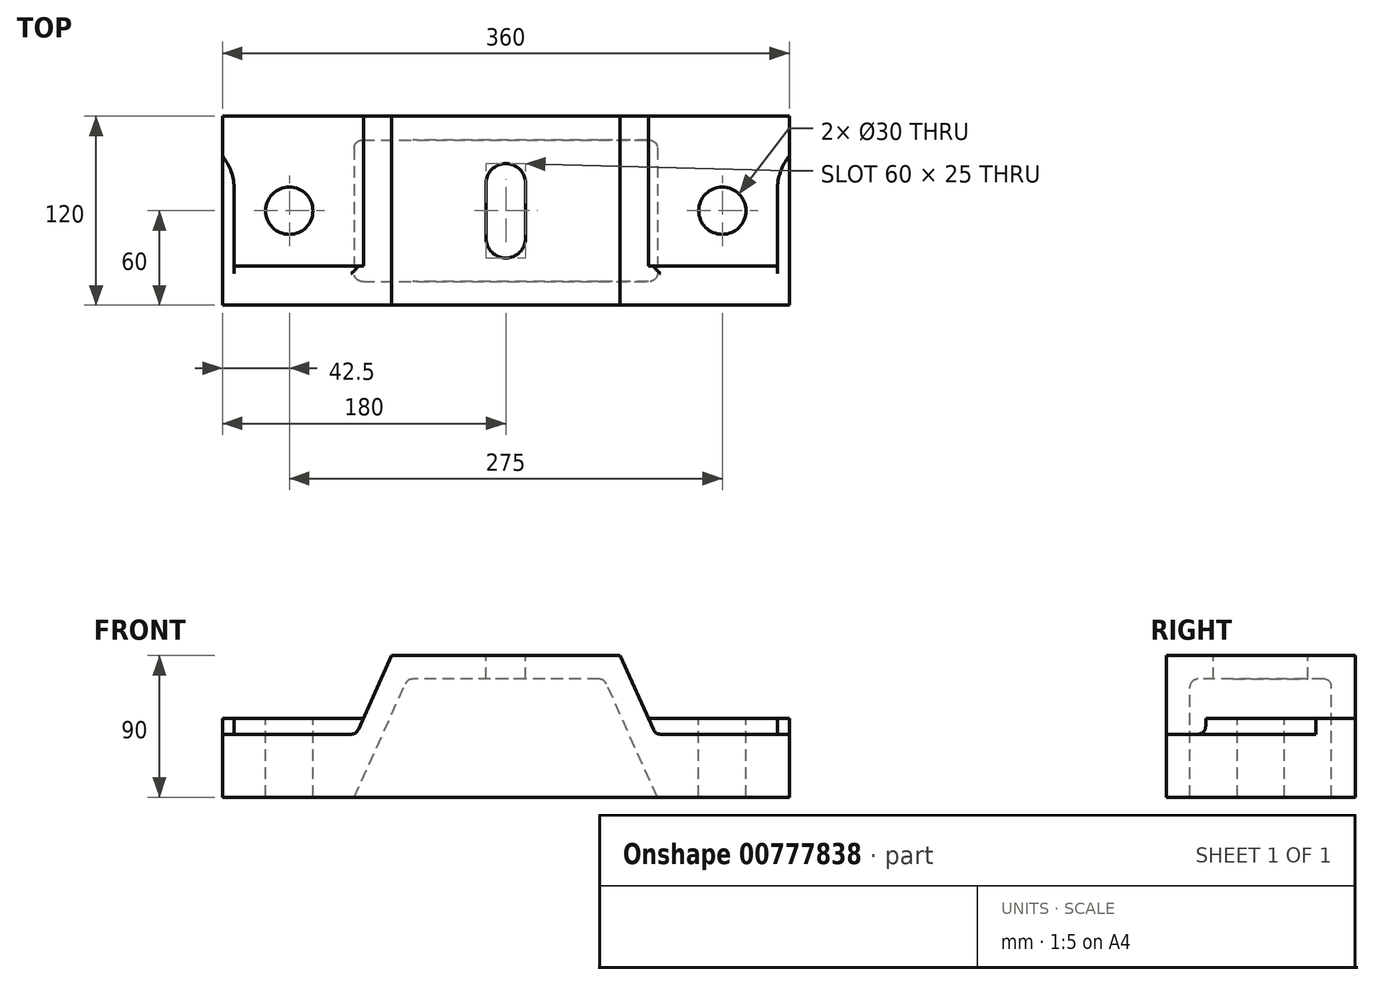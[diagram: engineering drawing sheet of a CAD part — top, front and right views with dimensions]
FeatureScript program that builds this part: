
annotation { "Feature Type Name" : "Feature", "Feature Type Description" : "" }
export const myFeature = defineFeature(function(context is Context, id is Id, definition is map)
    precondition{}
    {
        {
            var Q0;
            Q0=qCreatedBy(makeId("Front.planeOp"),FACE);
            var sketch = newSketch(context, id + "F0", { "sketchPlane" : qUnion([Q0])});
            skLineSegment(sketch, "E0", {"start": v(0, 0) * mm, "end": v(-180, 0) * mm});
            skLineSegment(sketch, "E1", {"start": v(-180, 0) * mm, "end": v(-180, 50) * mm});
            skLineSegment(sketch, "E2", {"start": v(-180, 50) * mm, "end": v(-90.5, 50) * mm});
            skLineSegment(sketch, "E3", {"start": v(-90.5, 50) * mm, "end": v(-72.5, 90) * mm});
            skLineSegment(sketch, "E4", {"start": v(-72.5, 90) * mm, "end": v(0, 90) * mm});
            skLineSegment(sketch, "E5", {"start": v(-90.5, 50) * mm, "end": v(-95, 40) * mm, "construction": true});
            skLineSegment(sketch, "E6.MirrorCS", {"start": v(72.5, 90) * mm, "end": v(0, 90) * mm});
            skLineSegment(sketch, "E7.MirrorCS", {"start": v(90.5, 50) * mm, "end": v(72.5, 90) * mm});
            skLineSegment(sketch, "E8.MirrorCS", {"start": v(180, 50) * mm, "end": v(90.5, 50) * mm});
            skLineSegment(sketch, "E9.MirrorCS", {"start": v(180, 0) * mm, "end": v(180, 50) * mm});
            skLineSegment(sketch, "E10.MirrorCS", {"start": v(0, 0) * mm, "end": v(180, 0) * mm});
            skSolve(sketch);
        }
        {
            var Q0;
            Q0=makeQuery(id+"F0.imprint","IMPRINT",FACE,{"disambiguationData":[TD([[makeQuery(id+"F0.imprint","IMPRINT",EDGE,{"derivedFrom":sQuery(id+"F0.wireOp",EDGE,"E0")}),-1.0]])]});
            extrude(context, id + "F1", {"entities" : qUnion([Q0]), "endBound" : BoundingType.SYMMETRIC, "depth" : 120 * mm, "offsetDistance" : 25 * mm});
        }
        {
            var Q0;
            Q0=makeQuery(id+"F1.opExtrude","CAP_FACE",FACE,{"disambiguationData":[OSD([sQuery(id+"F0.wireOp",EDGE,"E0"),sQuery(id+"F0.wireOp",EDGE,"E1"),sQuery(id+"F0.wireOp",EDGE,"E2"),sQuery(id+"F0.wireOp",EDGE,"E3"),sQuery(id+"F0.wireOp",EDGE,"E4"),sQuery(id+"F0.wireOp",EDGE,"E6.MirrorCS"),sQuery(id+"F0.wireOp",EDGE,"E7.MirrorCS"),sQuery(id+"F0.wireOp",EDGE,"E8.MirrorCS"),sQuery(id+"F0.wireOp",EDGE,"E9.MirrorCS"),sQuery(id+"F0.wireOp",EDGE,"E10.MirrorCS")])],"isStart":false});
            var sketch = newSketch(context, id + "F2", { "sketchPlane" : qUnion([Q0])});
            skLineSegment(sketch, "E11", {"start": v(-90.5, 50) * mm, "end": v(-95, 40) * mm});
            skLineSegment(sketch, "E12", {"start": v(-95, 40) * mm, "end": v(-180, 40) * mm});
            skLineSegment(sketch, "E13", {"start": v(-180, 40) * mm, "end": v(-180, 50) * mm});
            skLineSegment(sketch, "E14", {"start": v(-180, 50) * mm, "end": v(-90.5, 50) * mm});
            skLineSegment(sketch, "E15.MirrorCS", {"start": v(90.5, 50) * mm, "end": v(95, 40) * mm});
            skLineSegment(sketch, "E16.MirrorCS", {"start": v(95, 40) * mm, "end": v(180, 40) * mm});
            skLineSegment(sketch, "E17.MirrorCS", {"start": v(180, 40) * mm, "end": v(180, 50) * mm});
            skLineSegment(sketch, "E18.MirrorCS", {"start": v(180, 50) * mm, "end": v(90.5, 50) * mm});
            skSolve(sketch);
        }
        {
            var Q0;
            Q0 = qSketchRegion(id + "F2", true);
            extrude(context, id + "F3", {"entities" : qUnion([Q0]), "operationType" : NewBodyOperationType.REMOVE, "oppositeDirection" : true, "depth" : 25 * mm, "offsetDistance" : 25 * mm});
        }
        {
            var Q0;
            Q0=makeQuery(id+"F3.boolean.opBoolean","COPY",FACE,{"derivedFrom":makeQuery(id+"F3.opExtrude","CAP_FACE",FACE,{"disambiguationData":[OSD([sQuery(id+"F2.wireOp",EDGE,"E11"),sQuery(id+"F2.wireOp",EDGE,"E12"),sQuery(id+"F2.wireOp",EDGE,"E13"),sQuery(id+"F2.wireOp",EDGE,"E14")])],"isStart":false})});
            var sketch = newSketch(context, id + "F4", { "sketchPlane" : qUnion([Q0])});
            skLineSegment(sketch, "E19.bottom", {"start": v(-180, 40) * mm, "end": v(-172.5, 40) * mm});
            skLineSegment(sketch, "E19.top", {"start": v(-180, 50) * mm, "end": v(-172.5, 50) * mm});
            skLineSegment(sketch, "E19.left", {"start": v(-180, 40) * mm, "end": v(-180, 50) * mm});
            skLineSegment(sketch, "E19.right", {"start": v(-172.5, 40) * mm, "end": v(-172.5, 50) * mm});
            skLineSegment(sketch, "E20.MirrorCS", {"start": v(172.5, 40) * mm, "end": v(172.5, 50) * mm});
            skLineSegment(sketch, "E21.MirrorCS", {"start": v(180, 40) * mm, "end": v(172.5, 40) * mm});
            skLineSegment(sketch, "E22.MirrorCS", {"start": v(180, 40) * mm, "end": v(180, 50) * mm});
            skLineSegment(sketch, "E23.MirrorCS", {"start": v(180, 50) * mm, "end": v(172.5, 50) * mm});
            skSolve(sketch);
        }
        {
            var Q0;
            Q0 = qSketchRegion(id + "F4", true);
            extrude(context, id + "F5", {"entities" : qUnion([Q0]), "operationType" : NewBodyOperationType.REMOVE, "oppositeDirection" : true, "depth" : 70 * mm, "offsetDistance" : 25 * mm});
        }
        {
            var Q0;
            Q0=makeQuery(id+"F5.boolean.opBoolean","COPY",EDGE,{"derivedFrom":makeQuery(id+"F5.opExtrude","CAP_EDGE",EDGE,{"disambiguationData":[OSD([sQuery(id+"F4.wireOp",EDGE,"E20.MirrorCS")])],"isStart":true})});
            var Q1;
            Q1=makeQuery(id+"F5.boolean.opBoolean","COPY",EDGE,{"derivedFrom":makeQuery(id+"F5.opExtrude","CAP_EDGE",EDGE,{"disambiguationData":[OSD([sQuery(id+"F4.wireOp",EDGE,"E20.MirrorCS")])],"isStart":false})});
            var Q2;
            Q2=makeQuery(id+"F5.boolean.opBoolean","COPY",EDGE,{"derivedFrom":makeQuery(id+"F5.opExtrude","CAP_EDGE",EDGE,{"disambiguationData":[OSD([sQuery(id+"F4.wireOp",EDGE,"E19.right")])],"isStart":true})});
            var Q3;
            Q3=makeQuery(id+"F5.boolean.opBoolean","COPY",EDGE,{"derivedFrom":makeQuery(id+"F5.opExtrude","CAP_EDGE",EDGE,{"disambiguationData":[OSD([sQuery(id+"F4.wireOp",EDGE,"E19.right")])],"isStart":false})});
            fillet(context, id + "F6", {"entities" : qUnion([Q0, Q1, Q2, Q3]), "radius" : 35 * mm, "tangentPropagation" : true, "allowEdgeOverflow" : false});
        }
        {
            var Q0;
            Q0=makeQuery(id+"F3.boolean.opBoolean","COPY",EDGE,{"derivedFrom":makeQuery(id+"F3.opExtrude","CAP_EDGE",EDGE,{"disambiguationData":[OSD([sQuery(id+"F2.wireOp",EDGE,"E16.MirrorCS")])],"isStart":false})});
            var Q1;
            Q1=makeQuery(id+"F3.boolean.opBoolean","COPY",EDGE,{"derivedFrom":makeQuery(id+"F3.opExtrude","SWEPT_EDGE",EDGE,{"disambiguationData":[OSD([sQuery(id+"F2.wireOp",EDGE,"E15.MirrorCS"),sQuery(id+"F2.wireOp",EDGE,"E16.MirrorCS")])]})});
            var Q2;
            Q2=makeQuery(id+"FUGxs0qXSOKFCMJ_1.1.F3.boolean.opBoolean","COPY",EDGE,{"derivedFrom":makeQuery(id+"FUGxs0qXSOKFCMJ_1.1.F3.opExtrude","SWEPT_EDGE",EDGE,{"disambiguationData":[OSD([sQuery(id+"F2.wireOp",EDGE,"E15.MirrorCS"),sQuery(id+"F2.wireOp",EDGE,"E16.MirrorCS")])]})});
            var Q3;
            Q3=makeQuery(id+"F3.boolean.opBoolean","COPY",EDGE,{"derivedFrom":makeQuery(id+"F3.opExtrude","CAP_EDGE",EDGE,{"disambiguationData":[OSD([sQuery(id+"F2.wireOp",EDGE,"E12")])],"isStart":false})});
            var Q4;
            Q4=makeQuery(id+"F3.boolean.opBoolean","COPY",EDGE,{"derivedFrom":makeQuery(id+"F3.opExtrude","SWEPT_EDGE",EDGE,{"disambiguationData":[OSD([sQuery(id+"F2.wireOp",EDGE,"E11"),sQuery(id+"F2.wireOp",EDGE,"E12")])]})});
            var Q5;
            Q5=makeQuery(id+"FUGxs0qXSOKFCMJ_1.1.F3.boolean.opBoolean","COPY",EDGE,{"derivedFrom":makeQuery(id+"FUGxs0qXSOKFCMJ_1.1.F3.opExtrude","SWEPT_EDGE",EDGE,{"disambiguationData":[OSD([sQuery(id+"F2.wireOp",EDGE,"E11"),sQuery(id+"F2.wireOp",EDGE,"E12")])]})});
            fillet(context, id + "F7", {"entities" : qUnion([Q0, Q1, Q2, Q3, Q4, Q5]), "radius" : 5 * mm, "tangentPropagation" : true, "allowEdgeOverflow" : false});
        }
        {
            var Q0;
            Q0=makeQuery(id+"F1.opExtrude","SWEPT_FACE",FACE,{"disambiguationData":[OSD([sQuery(id+"F0.wireOp",EDGE,"E2")])]});
            var sketch = newSketch(context, id + "F8", { "sketchPlane" : qUnion([Q0])});
            skCircle(sketch, "E24", {"center": v(-137.5, 0) * mm, "radius": 15 * mm});
            skCircle(sketch, "E25", {"center": v(137.5, 0) * mm, "radius": 15 * mm});
            skSolve(sketch);
        }
        {
            var Q0;
            Q0=makeQuery(id+"F8.imprint","IMPRINT",FACE,{"disambiguationData":[TD([[makeQuery(id+"F8.imprint","IMPRINT",EDGE,{"derivedFrom":sQuery(id+"F8.wireOp",EDGE,"E24")}),1.0]])]});
            var Q1;
            Q1=makeQuery(id+"F8.imprint","IMPRINT",FACE,{"disambiguationData":[TD([[makeQuery(id+"F8.imprint","IMPRINT",EDGE,{"derivedFrom":sQuery(id+"F8.wireOp",EDGE,"E25")}),1.0]])]});
            extrude(context, id + "F9", {"entities" : qUnion([Q0, Q1]), "operationType" : NewBodyOperationType.REMOVE, "oppositeDirection" : true, "depth" : 50 * mm, "offsetDistance" : 25 * mm});
        }
        {
            var Q0;
            Q0=makeQuery(id+"F1.opExtrude","SWEPT_FACE",FACE,{"disambiguationData":[OSD([sQuery(id+"F0.wireOp",EDGE,"E4"),sQuery(id+"F0.wireOp",EDGE,"E6.MirrorCS")])]});
            var sketch = newSketch(context, id + "F10", { "sketchPlane" : qUnion([Q0])});
            skLineSegment(sketch, "E26.bottom", {"start": v(0, 30) * mm, "end": v(0, 30) * mm});
            skLineSegment(sketch, "E26.top", {"start": v(0, -30) * mm, "end": v(0, -30) * mm});
            skLineSegment(sketch, "E26.left", {"start": v(-12.5, 17.5) * mm, "end": v(-12.5, -17.5) * mm});
            skLineSegment(sketch, "E26.right", {"start": v(12.5, 17.5) * mm, "end": v(12.5, -17.5) * mm});
            skPoint(sketch, "E27.visualSharp", {"position": v(-12.5, 30) * mm});
            skArc(sketch, "E27.filletArc", {"start": v(0, 30) * mm, "mid": v(-8.84, 26.34) * mm, "end": v(-12.5, 17.5) * mm});
            skPoint(sketch, "E28.visualSharp", {"position": v(12.5, 30) * mm});
            skArc(sketch, "E28.filletArc", {"start": v(12.5, 17.5) * mm, "mid": v(8.84, 26.34) * mm, "end": v(0, 30) * mm});
            skPoint(sketch, "E29.visualSharp", {"position": v(12.5, -30) * mm});
            skArc(sketch, "E29.filletArc", {"start": v(0, -30) * mm, "mid": v(8.84, -26.34) * mm, "end": v(12.5, -17.5) * mm});
            skPoint(sketch, "E30.visualSharp", {"position": v(-12.5, -30) * mm});
            skArc(sketch, "E30.filletArc", {"start": v(-12.5, -17.5) * mm, "mid": v(-8.84, -26.34) * mm, "end": v(0, -30) * mm});
            skSolve(sketch);
        }
        {
            var Q0;
            Q0=makeQuery(id+"F10.imprint","IMPRINT",FACE,{"disambiguationData":[TD([[makeQuery(id+"F10.imprint","IMPRINT",EDGE,{"derivedFrom":sQuery(id+"F10.wireOp",EDGE,"E26.left")}),1.0]])]});
            extrude(context, id + "F11", {"entities" : qUnion([Q0]), "operationType" : NewBodyOperationType.REMOVE, "oppositeDirection" : true, "depth" : 90 * mm, "offsetDistance" : 25 * mm});
        }
        {
            var Q0;
            Q0=qCreatedBy(makeId("Front.planeOp"),FACE);
            var sketch = newSketch(context, id + "F12", { "sketchPlane" : qUnion([Q0])});
            skLineSegment(sketch, "E31", {"start": v(-96.25, 0) * mm, "end": v(-62.5, 75) * mm});
            skLineSegment(sketch, "E32", {"start": v(-62.5, 75) * mm, "end": v(0, 75) * mm});
            skLineSegment(sketch, "E33", {"start": v(-96.25, 0) * mm, "end": v(0, 0) * mm});
            skLineSegment(sketch, "E34.MirrorCS", {"start": v(62.5, 75) * mm, "end": v(0, 75) * mm});
            skLineSegment(sketch, "E35.MirrorCS", {"start": v(96.25, 0) * mm, "end": v(62.5, 75) * mm});
            skLineSegment(sketch, "E36.MirrorCS", {"start": v(96.25, 0) * mm, "end": v(0, 0) * mm});
            skSolve(sketch);
        }
        {
            var Q0;
            Q0 = qSketchRegion(id + "F12", true);
            extrude(context, id + "F13", {"entities" : qUnion([Q0]), "operationType" : NewBodyOperationType.REMOVE, "endBound" : BoundingType.SYMMETRIC, "oppositeDirection" : true, "depth" : 90 * mm, "offsetDistance" : 25 * mm});
        }
        {
            var Q0;
            Q0=makeQuery(id+"F13.boolean.opBoolean","COPY",EDGE,{"derivedFrom":makeQuery(id+"F13.opExtrude","CAP_EDGE",EDGE,{"disambiguationData":[OSD([sQuery(id+"F12.wireOp",EDGE,"E35.MirrorCS")])],"isStart":true})});
            var Q1;
            Q1=makeQuery(id+"F13.boolean.opBoolean","COPY",EDGE,{"derivedFrom":makeQuery(id+"F13.opExtrude","CAP_EDGE",EDGE,{"disambiguationData":[OSD([sQuery(id+"F12.wireOp",EDGE,"E32"),sQuery(id+"F12.wireOp",EDGE,"E34.MirrorCS")])],"isStart":true})});
            var Q2;
            Q2=makeQuery(id+"F13.boolean.opBoolean","COPY",EDGE,{"derivedFrom":makeQuery(id+"F13.opExtrude","SWEPT_EDGE",EDGE,{"disambiguationData":[OSD([sQuery(id+"F12.wireOp",EDGE,"E34.MirrorCS"),sQuery(id+"F12.wireOp",EDGE,"E35.MirrorCS")])]})});
            var Q3;
            Q3=makeQuery(id+"F13.boolean.opBoolean","COPY",EDGE,{"derivedFrom":makeQuery(id+"F13.opExtrude","SWEPT_EDGE",EDGE,{"disambiguationData":[OSD([sQuery(id+"F12.wireOp",EDGE,"E31"),sQuery(id+"F12.wireOp",EDGE,"E32")])]})});
            var Q4;
            Q4=makeQuery(id+"F13.boolean.opBoolean","COPY",EDGE,{"derivedFrom":makeQuery(id+"F13.opExtrude","CAP_EDGE",EDGE,{"disambiguationData":[OSD([sQuery(id+"F12.wireOp",EDGE,"E31")])],"isStart":true})});
            var Q5;
            Q5=makeQuery(id+"F13.boolean.opBoolean","COPY",EDGE,{"derivedFrom":makeQuery(id+"F13.opExtrude","CAP_EDGE",EDGE,{"disambiguationData":[OSD([sQuery(id+"F12.wireOp",EDGE,"E31")])],"isStart":false})});
            var Q6;
            Q6=makeQuery(id+"F13.boolean.opBoolean","COPY",EDGE,{"derivedFrom":makeQuery(id+"F13.opExtrude","CAP_EDGE",EDGE,{"disambiguationData":[OSD([sQuery(id+"F12.wireOp",EDGE,"E32"),sQuery(id+"F12.wireOp",EDGE,"E34.MirrorCS")])],"isStart":false})});
            var Q7;
            Q7=makeQuery(id+"F13.boolean.opBoolean","COPY",EDGE,{"derivedFrom":makeQuery(id+"F13.opExtrude","CAP_EDGE",EDGE,{"disambiguationData":[OSD([sQuery(id+"F12.wireOp",EDGE,"E35.MirrorCS")])],"isStart":false})});
            fillet(context, id + "F14", {"entities" : qUnion([Q0, Q1, Q2, Q3, Q4, Q5, Q6, Q7]), "radius" : 5 * mm, "tangentPropagation" : true, "allowEdgeOverflow" : false});
        }
    });
